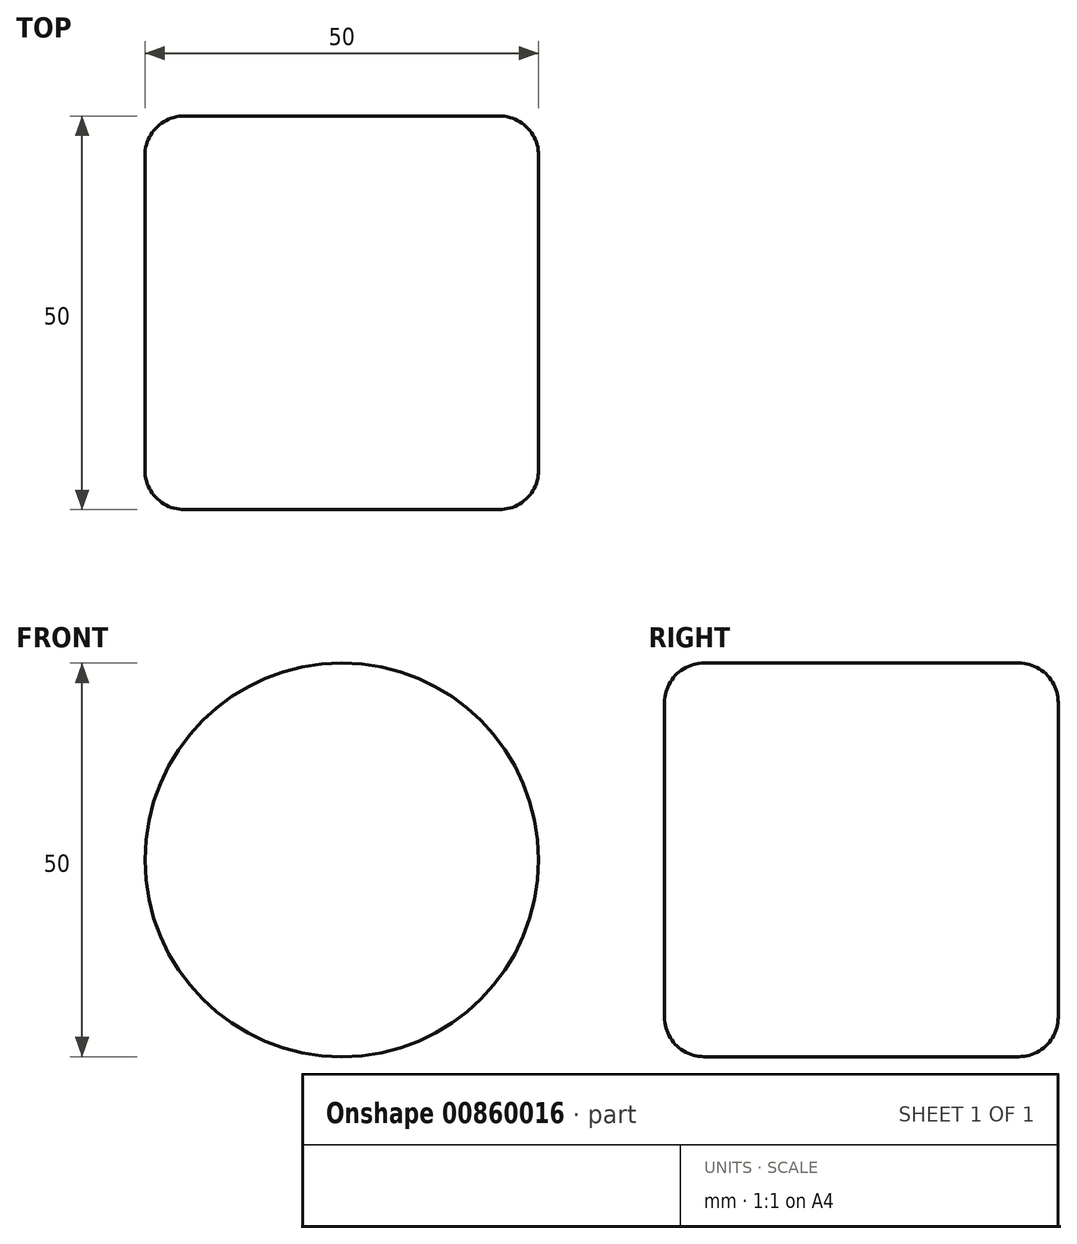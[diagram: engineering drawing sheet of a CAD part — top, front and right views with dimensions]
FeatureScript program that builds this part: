
annotation { "Feature Type Name" : "Feature", "Feature Type Description" : "" }
export const myFeature = defineFeature(function(context is Context, id is Id, definition is map)
    precondition{}
    {
        {
            var Q0;
            Q0=qCreatedBy(makeId("Front.planeOp"),FACE);
            var sketch = newSketch(context, id + "F0", { "sketchPlane" : qUnion([Q0])});
            skCircle(sketch, "E0", {"center": v(0, 0) * mm, "radius": 25 * mm});
            skSolve(sketch);
        }
        {
            var Q0;
            Q0=makeQuery(id+"F0.imprint","IMPRINT",FACE,{"disambiguationData":[TD([[makeQuery(id+"F0.imprint","IMPRINT",EDGE,{"derivedFrom":sQuery(id+"F0.wireOp",EDGE,"E0")}),1.0]])]});
            extrude(context, id + "F1", {"entities" : qUnion([Q0]), "depth" : 50 * mm, "offsetDistance" : 25 * mm});
        }
        {
            var Q0;
            Q0=makeQuery(id+"F1.opExtrude","CAP_EDGE",EDGE,{"disambiguationData":[OSD([sQuery(id+"F0.wireOp",EDGE,"E0")])],"isStart":true});
            var Q1;
            Q1=makeQuery(id+"F1.opExtrude","CAP_EDGE",EDGE,{"disambiguationData":[OSD([sQuery(id+"F0.wireOp",EDGE,"E0")])],"isStart":false});
            fillet(context, id + "F2", {"entities" : qUnion([Q0, Q1]), "tangentPropagation" : true, "radius" : 5 * mm, "defaultsChanged" : false, "vertexSettings" : [], "allowEdgeOverflow" : false});
        }
    });
